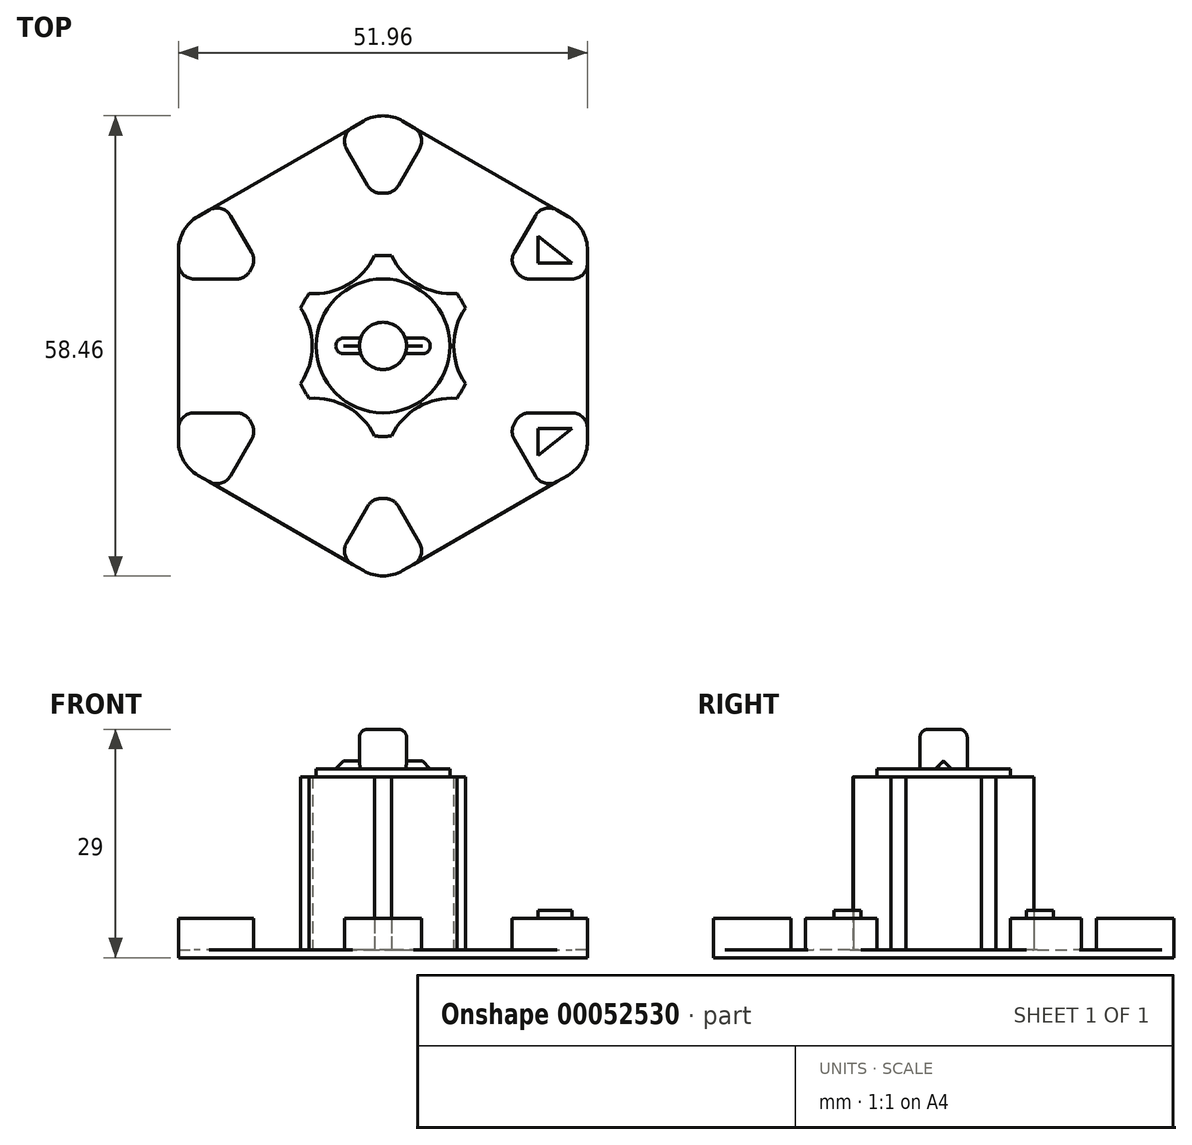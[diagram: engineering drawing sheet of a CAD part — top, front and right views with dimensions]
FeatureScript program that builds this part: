
annotation { "Feature Type Name" : "Feature", "Feature Type Description" : "" }
export const myFeature = defineFeature(function(context is Context, id is Id, definition is map)
    precondition{}
    {
        {
            var Q0;
            Q0=qCreatedBy(makeId("Top.planeOp"),FACE);
            var sketch = newSketch(context, id + "F0", { "sketchPlane" : qUnion([Q0])});
            skCircle(sketch, "E0", {"center": v(0, 0) * mm, "radius": 30 * mm, "construction": true});
            skLineSegment(sketch, "E1.0", {"start": v(0, 30) * mm, "end": v(25.98, 15) * mm});
            skLineSegment(sketch, "E1.1", {"start": v(25.98, 15) * mm, "end": v(25.98, -15) * mm});
            skLineSegment(sketch, "E1.2", {"start": v(25.98, -15) * mm, "end": v(0, -30) * mm});
            skLineSegment(sketch, "E1.3", {"start": v(0, -30) * mm, "end": v(-25.98, -15) * mm});
            skLineSegment(sketch, "E1.4", {"start": v(-25.98, -15) * mm, "end": v(-25.98, 15) * mm});
            skLineSegment(sketch, "E1.5", {"start": v(-25.98, 15) * mm, "end": v(0, 30) * mm});
            skSolve(sketch);
        }
        {
            var Q0;
            Q0 = qSketchRegion(id + "F0", true);
            var Q1;
            Q1=makeQuery(id+"F0.imprint","IMPRINT",FACE,{"disambiguationData":[TD([[makeQuery(id+"F0.imprint","IMPRINT",EDGE,{"derivedFrom":sQuery(id+"F0.wireOp",EDGE,"E1.0")}),-1.0]])]});
            extrude(context, id + "F1", {"entities" : qUnion([Q0, Q1]), "depth" : 1 * mm});
        }
        {
            var Q0;
            Q0=makeQuery(id+"F1.opExtrude","CAP_FACE",FACE,{"disambiguationData":[OSD([sQuery(id+"F0.wireOp",EDGE,"E1.0"),sQuery(id+"F0.wireOp",EDGE,"E1.1"),sQuery(id+"F0.wireOp",EDGE,"E1.2"),sQuery(id+"F0.wireOp",EDGE,"E1.3"),sQuery(id+"F0.wireOp",EDGE,"E1.4"),sQuery(id+"F0.wireOp",EDGE,"E1.5")])],"isStart":false});
            var sketch = newSketch(context, id + "F2", { "sketchPlane" : qUnion([Q0])});
            skLineSegment(sketch, "E2", {"start": v(25.98, -15) * mm, "end": v(25.98, 15) * mm});
            skLineSegment(sketch, "E3", {"start": v(0, 0) * mm, "end": v(17.48, 0) * mm, "construction": true});
            skCircle(sketch, "E4", {"center": v(17.48, 0) * mm, "radius": 8.5 * mm});
            skLineSegment(sketch, "E5.0", {"start": v(0, 30) * mm, "end": v(25.98, 15) * mm});
            skLineSegment(sketch, "E6.0", {"start": v(-25.98, 15) * mm, "end": v(0, 30) * mm});
            skLineSegment(sketch, "E7.0", {"start": v(0, -30) * mm, "end": v(-25.98, -15) * mm});
            skLineSegment(sketch, "E8.0", {"start": v(25.98, -15) * mm, "end": v(0, -30) * mm});
            skLineSegment(sketch, "E9.0", {"start": v(-25.98, -15) * mm, "end": v(-25.98, 15) * mm});
            skCircle(sketch, "E10.1.0", {"center": v(8.74, 15.14) * mm, "radius": 8.5 * mm});
            skCircle(sketch, "E10.2.0", {"center": v(-8.74, 15.14) * mm, "radius": 8.5 * mm});
            skCircle(sketch, "E10.3.0", {"center": v(-17.48, 0) * mm, "radius": 8.5 * mm});
            skCircle(sketch, "E10.4.0", {"center": v(-8.74, -15.14) * mm, "radius": 8.5 * mm});
            skCircle(sketch, "E10.5.0", {"center": v(8.74, -15.14) * mm, "radius": 8.5 * mm});
            skPoint(sketch, "E10.center", {"position": v(0, 0) * mm});
            skLineSegment(sketch, "E11", {"start": v(0, 0) * mm, "end": v(25.98, 15) * mm, "construction": true});
            skLineSegment(sketch, "E12", {"start": v(0, 0) * mm, "end": v(25.98, -15) * mm, "construction": true});
            skCircle(sketch, "E13", {"center": v(0, 0) * mm, "radius": 11.5 * mm});
            skSolve(sketch);
        }
        {
            var Q0;
            {var subQ3=sQuery(id+"F2.wireOp",EDGE,"5aa6aa30-cbac-45e4-aae3-3f16d059a961");Q0=makeQuery(id+"F2.imprint","IMPRINT",FACE,{"disambiguationData":[TD([[makeQuery(id+"F2.imprint","IMPRINT",EDGE,{"derivedFrom":subQ3}),1.0]])]});}
            var Q1;
            {var subQ0=sQuery(id+"F2.wireOp",EDGE,"E13");var subQ8=sQuery(id+"F2.wireOp",EDGE,"E4");var subQ9=makeQuery(id+"F2.imprint","INTERSECT",VERTEX,{"disambiguationData":[OD(0.0)],"derivedFrom":[subQ8,subQ0]});Q1=makeQuery(id+"F2.imprint","IMPRINT",FACE,{"disambiguationData":[TD([[makeQuery(id+"F2.imprint","IMPRINT",EDGE,{"disambiguationData":[TD([[subQ9,-1.0]])],"derivedFrom":subQ8}),-1.0]])]});}
            extrude(context, id + "F3", {"entities" : qUnion([Q0, Q1]), "operationType" : NewBodyOperationType.ADD, "depth" : 22 * mm});
        }
        {
            var Q0;
            Q0=makeQuery(id+"F1.opExtrude","CAP_FACE",FACE,{"disambiguationData":[OSD([sQuery(id+"F0.wireOp",EDGE,"E1.0"),sQuery(id+"F0.wireOp",EDGE,"E1.1"),sQuery(id+"F0.wireOp",EDGE,"E1.2"),sQuery(id+"F0.wireOp",EDGE,"E1.3"),sQuery(id+"F0.wireOp",EDGE,"E1.4"),sQuery(id+"F0.wireOp",EDGE,"E1.5")])],"isStart":false});
            var sketch = newSketch(context, id + "F4", { "sketchPlane" : qUnion([Q0])});
            skCircle(sketch, "E14", {"center": v(8.74, 15.14) * mm, "radius": 8.5 * mm, "construction": true});
            skArc(sketch, "E15.0", {"start": v(1.08, 11.45) * mm, "mid": v(4.5, 7.78) * mm, "end": v(9.37, 6.66) * mm});
            skArc(sketch, "E16.0", {"start": v(-9.37, 6.66) * mm, "mid": v(-4.5, 7.78) * mm, "end": v(-1.08, 11.45) * mm});
            skCircle(sketch, "E17", {"center": v(-8.74, 15.14) * mm, "radius": 8.5 * mm, "construction": true});
            skLineSegment(sketch, "E18", {"start": v(1.38, 19.39) * mm, "end": v(5.63, 26.75) * mm});
            skLineSegment(sketch, "E19.0", {"start": v(-25.98, 15) * mm, "end": v(0, 30) * mm, "construction": true});
            skLineSegment(sketch, "E20.0", {"start": v(0, 30) * mm, "end": v(25.98, 15) * mm, "construction": true});
            skLineSegment(sketch, "E21", {"start": v(0, 30) * mm, "end": v(0, 0) * mm, "construction": true});
            skLineSegment(sketch, "E22", {"start": v(1.38, 19.39) * mm, "end": v(-1.38, 19.39) * mm});
            skLineSegment(sketch, "E23", {"start": v(-1.38, 19.39) * mm, "end": v(-5.63, 26.75) * mm});
            skLineSegment(sketch, "E24", {"start": v(-5.63, 26.75) * mm, "end": v(0, 30) * mm});
            skLineSegment(sketch, "E25", {"start": v(0, 30) * mm, "end": v(5.63, 26.75) * mm});
            skLineSegment(sketch, "E26.1.0", {"start": v(-17.48, 8.5) * mm, "end": v(-25.98, 8.5) * mm});
            skLineSegment(sketch, "E26.1.1", {"start": v(-25.98, 8.5) * mm, "end": v(-25.98, 15) * mm});
            skLineSegment(sketch, "E26.1.2", {"start": v(-25.98, 15) * mm, "end": v(-20.35, 18.25) * mm});
            skLineSegment(sketch, "E26.1.3", {"start": v(-16.1, 10.89) * mm, "end": v(-20.35, 18.25) * mm});
            skLineSegment(sketch, "E26.1.4", {"start": v(-16.1, 10.89) * mm, "end": v(-17.48, 8.5) * mm});
            skLineSegment(sketch, "E26.2.0", {"start": v(-16.1, -10.89) * mm, "end": v(-20.35, -18.25) * mm});
            skLineSegment(sketch, "E26.2.1", {"start": v(-20.35, -18.25) * mm, "end": v(-25.98, -15) * mm});
            skLineSegment(sketch, "E26.2.2", {"start": v(-25.98, -15) * mm, "end": v(-25.98, -8.5) * mm});
            skLineSegment(sketch, "E26.2.3", {"start": v(-17.48, -8.5) * mm, "end": v(-25.98, -8.5) * mm});
            skLineSegment(sketch, "E26.2.4", {"start": v(-17.48, -8.5) * mm, "end": v(-16.1, -10.89) * mm});
            skLineSegment(sketch, "E26.3.0", {"start": v(1.38, -19.39) * mm, "end": v(5.63, -26.75) * mm});
            skLineSegment(sketch, "E26.3.1", {"start": v(5.63, -26.75) * mm, "end": v(0, -30) * mm});
            skLineSegment(sketch, "E26.3.2", {"start": v(0, -30) * mm, "end": v(-5.63, -26.75) * mm});
            skLineSegment(sketch, "E26.3.3", {"start": v(-1.38, -19.39) * mm, "end": v(-5.63, -26.75) * mm});
            skLineSegment(sketch, "E26.3.4", {"start": v(-1.38, -19.39) * mm, "end": v(1.38, -19.39) * mm});
            skLineSegment(sketch, "E26.4.0", {"start": v(17.48, -8.5) * mm, "end": v(25.98, -8.5) * mm});
            skLineSegment(sketch, "E26.4.1", {"start": v(25.98, -8.5) * mm, "end": v(25.98, -15) * mm});
            skLineSegment(sketch, "E26.4.2", {"start": v(25.98, -15) * mm, "end": v(20.35, -18.25) * mm});
            skLineSegment(sketch, "E26.4.3", {"start": v(16.1, -10.89) * mm, "end": v(20.35, -18.25) * mm});
            skLineSegment(sketch, "E26.4.4", {"start": v(16.1, -10.89) * mm, "end": v(17.48, -8.5) * mm});
            skLineSegment(sketch, "E26.5.0", {"start": v(16.1, 10.89) * mm, "end": v(20.35, 18.25) * mm});
            skLineSegment(sketch, "E26.5.1", {"start": v(20.35, 18.25) * mm, "end": v(25.98, 15) * mm});
            skLineSegment(sketch, "E26.5.2", {"start": v(25.98, 15) * mm, "end": v(25.98, 8.5) * mm});
            skLineSegment(sketch, "E26.5.3", {"start": v(17.48, 8.5) * mm, "end": v(25.98, 8.5) * mm});
            skLineSegment(sketch, "E26.5.4", {"start": v(17.48, 8.5) * mm, "end": v(16.1, 10.89) * mm});
            skPoint(sketch, "E26.center", {"position": v(0, 0) * mm});
            skSolve(sketch);
        }
        {
            var Q0;
            Q0=makeQuery(id+"F4.imprint","IMPRINT",FACE,{"disambiguationData":[TD([[makeQuery(id+"F4.imprint","IMPRINT",EDGE,{"derivedFrom":sQuery(id+"F4.wireOp",EDGE,"E18")}),1.0]])]});
            var Q1;
            Q1=makeQuery(id+"F4.imprint","IMPRINT",FACE,{"disambiguationData":[TD([[makeQuery(id+"F4.imprint","IMPRINT",EDGE,{"derivedFrom":sQuery(id+"F4.wireOp",EDGE,"E26.1.0")}),-1.0]])]});
            var Q2;
            Q2=makeQuery(id+"F4.imprint","IMPRINT",FACE,{"disambiguationData":[TD([[makeQuery(id+"F4.imprint","IMPRINT",EDGE,{"derivedFrom":sQuery(id+"F4.wireOp",EDGE,"E26.2.0")}),-1.0]])]});
            var Q3;
            Q3=makeQuery(id+"F4.imprint","IMPRINT",FACE,{"disambiguationData":[TD([[makeQuery(id+"F4.imprint","IMPRINT",EDGE,{"derivedFrom":sQuery(id+"F4.wireOp",EDGE,"E26.3.0")}),-1.0]])]});
            var Q4;
            Q4=makeQuery(id+"F4.imprint","IMPRINT",FACE,{"disambiguationData":[TD([[makeQuery(id+"F4.imprint","IMPRINT",EDGE,{"derivedFrom":sQuery(id+"F4.wireOp",EDGE,"E26.4.0")}),-1.0]])]});
            var Q5;
            Q5=makeQuery(id+"F4.imprint","IMPRINT",FACE,{"disambiguationData":[TD([[makeQuery(id+"F4.imprint","IMPRINT",EDGE,{"derivedFrom":sQuery(id+"F4.wireOp",EDGE,"E26.5.0")}),-1.0]])]});
            extrude(context, id + "F5", {"entities" : qUnion([Q0, Q1, Q2, Q3, Q4, Q5]), "operationType" : NewBodyOperationType.ADD, "depth" : 4 * mm});
        }
        {
            var Q0;
            Q0=makeQuery(id+"F5.opExtrude","SWEPT_EDGE",EDGE,{"disambiguationData":[OSD([sQuery(id+"F4.wireOp",EDGE,"E22"),sQuery(id+"F4.wireOp",EDGE,"E23")])]});
            var Q1;
            Q1=makeQuery(id+"F5.opExtrude","SWEPT_EDGE",EDGE,{"disambiguationData":[OSD([sQuery(id+"F4.wireOp",EDGE,"E18"),sQuery(id+"F4.wireOp",EDGE,"E22")])]});
            var Q2;
            Q2=makeQuery(id+"F5.opExtrude","SWEPT_EDGE",EDGE,{"disambiguationData":[OSD([sQuery(id+"F4.wireOp",EDGE,"E26.1.3"),sQuery(id+"F4.wireOp",EDGE,"E26.1.4")])]});
            var Q3;
            Q3=makeQuery(id+"F5.opExtrude","SWEPT_EDGE",EDGE,{"disambiguationData":[OSD([sQuery(id+"F4.wireOp",EDGE,"E26.1.0"),sQuery(id+"F4.wireOp",EDGE,"E26.1.4")])]});
            var Q4;
            Q4=makeQuery(id+"F5.opExtrude","SWEPT_EDGE",EDGE,{"disambiguationData":[OSD([sQuery(id+"F4.wireOp",EDGE,"E26.5.0"),sQuery(id+"F4.wireOp",EDGE,"E26.5.4")])]});
            var Q5;
            Q5=makeQuery(id+"F5.opExtrude","SWEPT_EDGE",EDGE,{"disambiguationData":[OSD([sQuery(id+"F4.wireOp",EDGE,"E26.5.3"),sQuery(id+"F4.wireOp",EDGE,"E26.5.4")])]});
            var Q6;
            Q6=makeQuery(id+"F5.opExtrude","SWEPT_EDGE",EDGE,{"disambiguationData":[OSD([sQuery(id+"F4.wireOp",EDGE,"E26.2.3"),sQuery(id+"F4.wireOp",EDGE,"E26.2.4")])]});
            var Q7;
            Q7=makeQuery(id+"F5.opExtrude","SWEPT_EDGE",EDGE,{"disambiguationData":[OSD([sQuery(id+"F4.wireOp",EDGE,"E26.2.0"),sQuery(id+"F4.wireOp",EDGE,"E26.2.4")])]});
            var Q8;
            Q8=makeQuery(id+"F5.opExtrude","SWEPT_EDGE",EDGE,{"disambiguationData":[OSD([sQuery(id+"F4.wireOp",EDGE,"E26.3.3"),sQuery(id+"F4.wireOp",EDGE,"E26.3.4")])]});
            var Q9;
            Q9=makeQuery(id+"F5.opExtrude","SWEPT_EDGE",EDGE,{"disambiguationData":[OSD([sQuery(id+"F4.wireOp",EDGE,"E26.3.0"),sQuery(id+"F4.wireOp",EDGE,"E26.3.4")])]});
            var Q10;
            Q10=makeQuery(id+"F5.opExtrude","SWEPT_EDGE",EDGE,{"disambiguationData":[OSD([sQuery(id+"F4.wireOp",EDGE,"E26.4.3"),sQuery(id+"F4.wireOp",EDGE,"E26.4.4")])]});
            var Q11;
            Q11=makeQuery(id+"F5.opExtrude","SWEPT_EDGE",EDGE,{"disambiguationData":[OSD([sQuery(id+"F4.wireOp",EDGE,"E26.4.0"),sQuery(id+"F4.wireOp",EDGE,"E26.4.4")])]});
            var Q12;
            Q12=makeQuery(id+"F5.opExtrude","SWEPT_EDGE",EDGE,{"disambiguationData":[OSD([sQuery(id+"F0.wireOp",EDGE,"E1.2"),sQuery(id+"F4.wireOp",EDGE,"E26.3.0"),sQuery(id+"F4.wireOp",EDGE,"E26.3.1")])]});
            var Q13;
            Q13=makeQuery(id+"F5.opExtrude","SWEPT_EDGE",EDGE,{"disambiguationData":[OSD([sQuery(id+"F0.wireOp",EDGE,"E1.2"),sQuery(id+"F4.wireOp",EDGE,"E26.4.2"),sQuery(id+"F4.wireOp",EDGE,"E26.4.3")])]});
            var Q14;
            Q14=makeQuery(id+"F5.opExtrude","SWEPT_EDGE",EDGE,{"disambiguationData":[OSD([sQuery(id+"F0.wireOp",EDGE,"E1.3"),sQuery(id+"F4.wireOp",EDGE,"E26.3.2"),sQuery(id+"F4.wireOp",EDGE,"E26.3.3")])]});
            var Q15;
            Q15=makeQuery(id+"F5.opExtrude","SWEPT_EDGE",EDGE,{"disambiguationData":[OSD([sQuery(id+"F0.wireOp",EDGE,"E1.3"),sQuery(id+"F4.wireOp",EDGE,"E26.2.0"),sQuery(id+"F4.wireOp",EDGE,"E26.2.1")])]});
            var Q16;
            Q16=makeQuery(id+"F5.opExtrude","SWEPT_EDGE",EDGE,{"disambiguationData":[OSD([sQuery(id+"F0.wireOp",EDGE,"E1.4"),sQuery(id+"F4.wireOp",EDGE,"E26.2.2"),sQuery(id+"F4.wireOp",EDGE,"E26.2.3")])]});
            var Q17;
            Q17=makeQuery(id+"F5.opExtrude","SWEPT_EDGE",EDGE,{"disambiguationData":[OSD([sQuery(id+"F0.wireOp",EDGE,"E1.4"),sQuery(id+"F4.wireOp",EDGE,"E26.1.0"),sQuery(id+"F4.wireOp",EDGE,"E26.1.1")])]});
            var Q18;
            Q18=makeQuery(id+"F5.opExtrude","SWEPT_EDGE",EDGE,{"disambiguationData":[OSD([sQuery(id+"F0.wireOp",EDGE,"E1.5"),sQuery(id+"F4.wireOp",EDGE,"E26.1.2"),sQuery(id+"F4.wireOp",EDGE,"E26.1.3")])]});
            var Q19;
            Q19=makeQuery(id+"F5.opExtrude","SWEPT_EDGE",EDGE,{"disambiguationData":[OSD([sQuery(id+"F0.wireOp",EDGE,"E1.5"),sQuery(id+"F4.wireOp",EDGE,"E23"),sQuery(id+"F4.wireOp",EDGE,"E24")])]});
            var Q20;
            Q20=makeQuery(id+"F5.opExtrude","SWEPT_EDGE",EDGE,{"disambiguationData":[OSD([sQuery(id+"F0.wireOp",EDGE,"E1.0"),sQuery(id+"F4.wireOp",EDGE,"E18"),sQuery(id+"F4.wireOp",EDGE,"E25")])]});
            var Q21;
            Q21=makeQuery(id+"F5.opExtrude","SWEPT_EDGE",EDGE,{"disambiguationData":[OSD([sQuery(id+"F0.wireOp",EDGE,"E1.1"),sQuery(id+"F4.wireOp",EDGE,"E26.5.2"),sQuery(id+"F4.wireOp",EDGE,"E26.5.3")])]});
            var Q22;
            Q22=makeQuery(id+"F5.opExtrude","SWEPT_EDGE",EDGE,{"disambiguationData":[OSD([sQuery(id+"F0.wireOp",EDGE,"E1.1"),sQuery(id+"F4.wireOp",EDGE,"E26.4.0"),sQuery(id+"F4.wireOp",EDGE,"E26.4.1")])]});
            var Q23;
            Q23=makeQuery(id+"F5.opExtrude","SWEPT_EDGE",EDGE,{"disambiguationData":[OSD([sQuery(id+"F0.wireOp",EDGE,"E1.0"),sQuery(id+"F4.wireOp",EDGE,"E26.5.0"),sQuery(id+"F4.wireOp",EDGE,"E26.5.1")])]});
            fillet(context, id + "F6", {"entities" : qUnion([Q0, Q1, Q2, Q3, Q4, Q5, Q6, Q7, Q8, Q9, Q10, Q11, Q12, Q13, Q14, Q15, Q16, Q17, Q18, Q19, Q20, Q21, Q22, Q23]), "radius" : 2 * mm, "tangentPropagation" : true, "allowEdgeOverflow" : false});
        }
        {
            var Q0;
            Q0=makeQuery(id+"F5.boolean.opBoolean","MERGE",EDGE,{"derivedFrom":[makeQuery(id+"F1.opExtrude","SWEPT_EDGE",EDGE,{"disambiguationData":[OSD([sQuery(id+"F0.wireOp",EDGE,"E1.1"),sQuery(id+"F0.wireOp",EDGE,"E1.2")])]}),makeQuery(id+"F5.opExtrude","SWEPT_EDGE",EDGE,{"disambiguationData":[OSD([sQuery(id+"F4.wireOp",EDGE,"E26.4.1"),sQuery(id+"F4.wireOp",EDGE,"E26.4.2")])]})]});
            var Q1;
            Q1=makeQuery(id+"F5.boolean.opBoolean","MERGE",EDGE,{"derivedFrom":[makeQuery(id+"F1.opExtrude","SWEPT_EDGE",EDGE,{"disambiguationData":[OSD([sQuery(id+"F0.wireOp",EDGE,"E1.0"),sQuery(id+"F0.wireOp",EDGE,"E1.1")])]}),makeQuery(id+"F5.opExtrude","SWEPT_EDGE",EDGE,{"disambiguationData":[OSD([sQuery(id+"F4.wireOp",EDGE,"E26.5.1"),sQuery(id+"F4.wireOp",EDGE,"E26.5.2")])]})]});
            var Q2;
            Q2=makeQuery(id+"F5.boolean.opBoolean","MERGE",EDGE,{"derivedFrom":[makeQuery(id+"F1.opExtrude","SWEPT_EDGE",EDGE,{"disambiguationData":[OSD([sQuery(id+"F0.wireOp",EDGE,"E1.0"),sQuery(id+"F0.wireOp",EDGE,"E1.5")])]}),makeQuery(id+"F5.opExtrude","SWEPT_EDGE",EDGE,{"disambiguationData":[OSD([sQuery(id+"F4.wireOp",EDGE,"E24"),sQuery(id+"F4.wireOp",EDGE,"E25")])]})]});
            var Q3;
            Q3=makeQuery(id+"F5.boolean.opBoolean","MERGE",EDGE,{"derivedFrom":[makeQuery(id+"F1.opExtrude","SWEPT_EDGE",EDGE,{"disambiguationData":[OSD([sQuery(id+"F0.wireOp",EDGE,"E1.2"),sQuery(id+"F0.wireOp",EDGE,"E1.3")])]}),makeQuery(id+"F5.opExtrude","SWEPT_EDGE",EDGE,{"disambiguationData":[OSD([sQuery(id+"F4.wireOp",EDGE,"E26.3.1"),sQuery(id+"F4.wireOp",EDGE,"E26.3.2")])]})]});
            var Q4;
            Q4=makeQuery(id+"F5.boolean.opBoolean","MERGE",EDGE,{"derivedFrom":[makeQuery(id+"F1.opExtrude","SWEPT_EDGE",EDGE,{"disambiguationData":[OSD([sQuery(id+"F0.wireOp",EDGE,"E1.3"),sQuery(id+"F0.wireOp",EDGE,"E1.4")])]}),makeQuery(id+"F5.opExtrude","SWEPT_EDGE",EDGE,{"disambiguationData":[OSD([sQuery(id+"F4.wireOp",EDGE,"E26.2.1"),sQuery(id+"F4.wireOp",EDGE,"E26.2.2")])]})]});
            var Q5;
            Q5=makeQuery(id+"F5.boolean.opBoolean","MERGE",EDGE,{"derivedFrom":[makeQuery(id+"F1.opExtrude","SWEPT_EDGE",EDGE,{"disambiguationData":[OSD([sQuery(id+"F0.wireOp",EDGE,"E1.4"),sQuery(id+"F0.wireOp",EDGE,"E1.5")])]}),makeQuery(id+"F5.opExtrude","SWEPT_EDGE",EDGE,{"disambiguationData":[OSD([sQuery(id+"F4.wireOp",EDGE,"E26.1.1"),sQuery(id+"F4.wireOp",EDGE,"E26.1.2")])]})]});
            fillet(context, id + "F7", {"entities" : qUnion([Q0, Q1, Q2, Q3, Q4, Q5]), "radius" : 5 * mm, "tangentPropagation" : true, "allowEdgeOverflow" : false});
        }
        {
            var Q0;
            Q0=makeQuery(id+"F5.opExtrude","CAP_FACE",FACE,{"disambiguationData":[OSD([sQuery(id+"F4.wireOp",EDGE,"E26.5.0"),sQuery(id+"F4.wireOp",EDGE,"E26.5.1"),sQuery(id+"F4.wireOp",EDGE,"E26.5.2"),sQuery(id+"F4.wireOp",EDGE,"E26.5.3"),sQuery(id+"F4.wireOp",EDGE,"E26.5.4")])],"isStart":false});
            var sketch = newSketch(context, id + "F8", { "sketchPlane" : qUnion([Q0])});
            skLineSegment(sketch, "E27", {"start": v(23.98, 10.5) * mm, "end": v(19.66, 10.5) * mm});
            skLineSegment(sketch, "E28", {"start": v(19.66, 10.5) * mm, "end": v(19.66, 13.92) * mm});
            skLineSegment(sketch, "E29", {"start": v(19.66, 13.92) * mm, "end": v(23.98, 10.5) * mm});
            skLineSegment(sketch, "E30", {"start": v(0, 0) * mm, "end": v(25.98, 0) * mm, "construction": true});
            skLineSegment(sketch, "E31.MirrorCS", {"start": v(19.66, -13.92) * mm, "end": v(23.98, -10.5) * mm});
            skLineSegment(sketch, "E32.MirrorCS", {"start": v(19.66, -10.5) * mm, "end": v(19.66, -13.92) * mm});
            skLineSegment(sketch, "E33.MirrorCS", {"start": v(23.98, -10.5) * mm, "end": v(19.66, -10.5) * mm});
            skSolve(sketch);
        }
        {
            var Q0;
            Q0=makeQuery(id+"F8.imprint","IMPRINT",FACE,{"disambiguationData":[TD([[makeQuery(id+"F8.imprint","IMPRINT",EDGE,{"derivedFrom":sQuery(id+"F8.wireOp",EDGE,"E27")}),-1.0]])]});
            var Q1;
            Q1=makeQuery(id+"F8.imprint","IMPRINT",FACE,{"disambiguationData":[TD([[makeQuery(id+"F8.imprint","IMPRINT",EDGE,{"derivedFrom":sQuery(id+"F8.wireOp",EDGE,"E31.MirrorCS")}),1.0]])]});
            extrude(context, id + "F9", {"entities" : qUnion([Q0, Q1]), "operationType" : NewBodyOperationType.ADD, "depth" : 1 * mm});
        }
        {
            var Q0;
            Q0=makeQuery(id+"F3.opExtrude","CAP_FACE",FACE,{"disambiguationData":[OSD([sQuery(id+"F2.wireOp",EDGE,"E4"),sQuery(id+"F2.wireOp",EDGE,"E10.1.0"),sQuery(id+"F2.wireOp",EDGE,"E10.2.0"),sQuery(id+"F2.wireOp",EDGE,"E10.3.0"),sQuery(id+"F2.wireOp",EDGE,"E10.4.0"),sQuery(id+"F2.wireOp",EDGE,"E10.5.0"),sQuery(id+"F2.wireOp",EDGE,"E13")])],"isStart":false});
            var sketch = newSketch(context, id + "F10", { "sketchPlane" : qUnion([Q0])});
            skArc(sketch, "E34.0", {"start": v(10.46, 4.79) * mm, "mid": v(8.98, 0) * mm, "end": v(10.46, -4.79) * mm});
            skCircle(sketch, "E35", {"center": v(0, 0) * mm, "radius": 8.5 * mm});
            skCircle(sketch, "E36", {"center": v(0, 0) * mm, "radius": 3 * mm});
            skArc(sketch, "E37", {"start": v(5, -1) * mm, "mid": v(6, 0) * mm, "end": v(5, 1) * mm});
            skLineSegment(sketch, "E38", {"start": v(5, 1) * mm, "end": v(2.83, 1) * mm});
            skLineSegment(sketch, "E39", {"start": v(5, -1) * mm, "end": v(2.83, -1) * mm});
            skLineSegment(sketch, "E40", {"start": v(0, 0) * mm, "end": v(0, 3.99) * mm, "construction": true});
            skLineSegment(sketch, "E41.MirrorCS", {"start": v(-5, 1) * mm, "end": v(-2.83, 1) * mm});
            skArc(sketch, "E42.MirrorCS", {"start": v(-5, -1) * mm, "mid": v(-6, 0) * mm, "end": v(-5, 1) * mm});
            skLineSegment(sketch, "E43.MirrorCS", {"start": v(-5, -1) * mm, "end": v(-2.83, -1) * mm});
            skSolve(sketch);
        }
        {
            var Q0;
            Q0=makeQuery(id+"F10.imprint","IMPRINT",FACE,{"disambiguationData":[TD([[makeQuery(id+"F10.imprint","IMPRINT",EDGE,{"derivedFrom":sQuery(id+"F10.wireOp",EDGE,"E36")}),1.0]])]});
            extrude(context, id + "F11", {"entities" : qUnion([Q0]), "operationType" : NewBodyOperationType.ADD, "depth" : 6 * mm});
        }
        {
            var Q0;
            Q0=makeQuery(id+"F11.opExtrude","CAP_EDGE",EDGE,{"disambiguationData":[OSD([sQuery(id+"F10.wireOp",EDGE,"E36")])],"isStart":false});
            fillet(context, id + "F12", {"entities" : qUnion([Q0]), "radius" : 1 * mm, "tangentPropagation" : true, "allowEdgeOverflow" : false});
        }
        {
            var Q0;
            Q0=makeQuery(id+"F10.imprint","IMPRINT",FACE,{"disambiguationData":[TD([[makeQuery(id+"F10.imprint","IMPRINT",EDGE,{"derivedFrom":sQuery(id+"F10.wireOp",EDGE,"E35")}),1.0]])]});
            extrude(context, id + "F13", {"entities" : qUnion([Q0]), "operationType" : NewBodyOperationType.ADD, "depth" : 1 * mm});
        }
        {
            var Q0;
            {var subQ0=sQuery(id+"F10.wireOp",EDGE,"E41.MirrorCS");Q0=makeQuery(id+"F10.imprint","IMPRINT",FACE,{"disambiguationData":[TD([[makeQuery(id+"F10.imprint","IMPRINT",EDGE,{"derivedFrom":subQ0}),-1.0]])]});}
            var Q1;
            Q1=makeQuery(id+"F10.imprint","IMPRINT",FACE,{"disambiguationData":[TD([[makeQuery(id+"F10.imprint","IMPRINT",EDGE,{"derivedFrom":sQuery(id+"F10.wireOp",EDGE,"E37")}),1.0]])]});
            extrude(context, id + "F14", {"entities" : qUnion([Q0, Q1]), "operationType" : NewBodyOperationType.ADD, "depth" : 2 * mm});
        }
        {
            var Q0;
            Q0=makeQuery(id+"F14.opExtrude","CAP_EDGE",EDGE,{"disambiguationData":[OSD([sQuery(id+"F10.wireOp",EDGE,"E42.MirrorCS")])],"isStart":false});
            var Q1;
            Q1=makeQuery(id+"F14.opExtrude","CAP_EDGE",EDGE,{"disambiguationData":[OSD([sQuery(id+"F10.wireOp",EDGE,"E37")])],"isStart":false});
            chamfer(context, id + "F15", {"entities" : qUnion([Q0, Q1]), "width" : 1 * mm, "tangentPropagation" : true});
        }
    });
